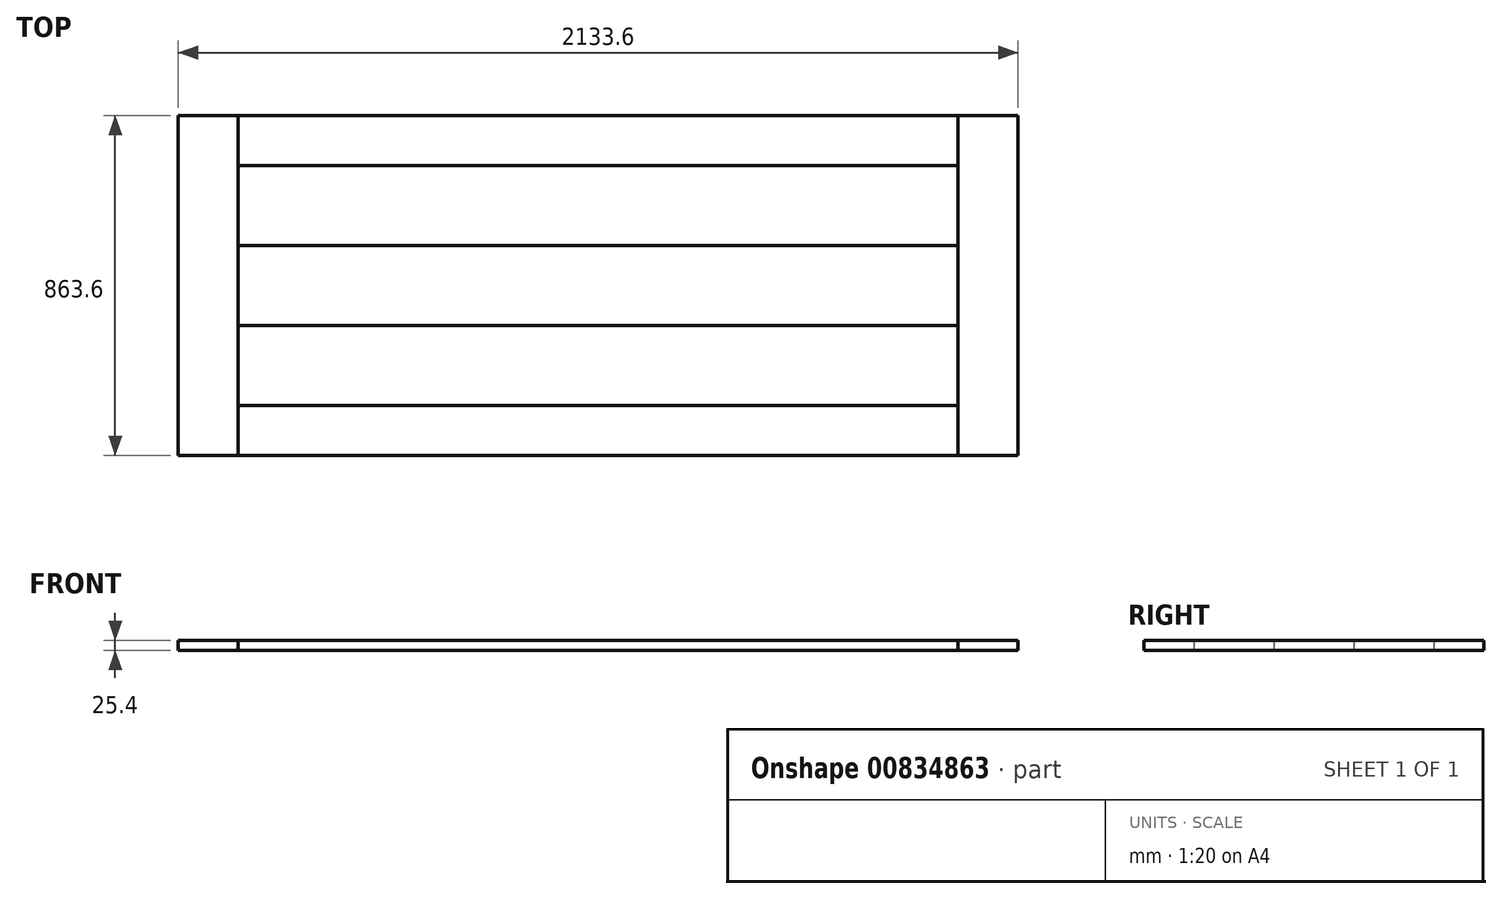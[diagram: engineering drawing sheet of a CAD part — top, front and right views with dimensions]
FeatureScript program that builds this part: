
annotation { "Feature Type Name" : "Feature", "Feature Type Description" : "" }
export const myFeature = defineFeature(function(context is Context, id is Id, definition is map)
    precondition{}
    {
        {
            var Q0;
            Q0=qCreatedBy(makeId("Top.planeOp"),FACE);
            var sketch = newSketch(context, id + "F0", { "sketchPlane" : qUnion([Q0])});
            skLineSegment(sketch, "E0.bottom", {"start": v(1066.8, -431.8) * mm, "end": v(-1066.8, -431.8) * mm});
            skLineSegment(sketch, "E0.top", {"start": v(1066.8, 431.8) * mm, "end": v(-1066.8, 431.8) * mm});
            skLineSegment(sketch, "E0.left", {"start": v(1066.8, -431.8) * mm, "end": v(1066.8, 431.8) * mm});
            skLineSegment(sketch, "E0.right", {"start": v(-1066.8, -431.8) * mm, "end": v(-1066.8, 431.8) * mm});
            skPoint(sketch, "E0.middle", {"position": v(0, 0) * mm});
            skLineSegment(sketch, "E1", {"start": v(-914.4, 431.8) * mm, "end": v(-914.4, -431.8) * mm});
            skLineSegment(sketch, "E2", {"start": v(914.4, 431.8) * mm, "end": v(914.4, -431.8) * mm});
            skLineSegment(sketch, "E3", {"start": v(-914.4, -304.8) * mm, "end": v(914.4, -304.8) * mm});
            skLineSegment(sketch, "E4", {"start": v(-914.4, -101.6) * mm, "end": v(914.4, -101.6) * mm});
            skLineSegment(sketch, "E5", {"start": v(-914.4, 101.6) * mm, "end": v(914.4, 101.6) * mm});
            skLineSegment(sketch, "E6", {"start": v(-914.4, 304.8) * mm, "end": v(914.4, 304.8) * mm});
            skSolve(sketch);
        }
        {
            var Q0;
            {var subQ4=sQuery(id+"F0.wireOp",EDGE,"E0.right");Q0=makeQuery(id+"F0.imprint","IMPRINT",FACE,{"disambiguationData":[TD([[makeQuery(id+"F0.imprint","IMPRINT",EDGE,{"derivedFrom":subQ4}),-1.0]])]});}
            var Q1;
            {var subQ0=sQuery(id+"F0.wireOp",EDGE,"E0.left");Q1=makeQuery(id+"F0.imprint","IMPRINT",FACE,{"disambiguationData":[TD([[makeQuery(id+"F0.imprint","IMPRINT",EDGE,{"derivedFrom":subQ0}),1.0]])]});}
            extrude(context, id + "F1", {"entities" : qUnion([Q0, Q1]), "depth" : 25.4 * mm, "offsetDistance" : 25.4 * mm});
        }
        {
            var Q0;
            {var subQ5=sQuery(id+"F0.wireOp",EDGE,"E6");Q0=makeQuery(id+"F0.imprint","IMPRINT",FACE,{"disambiguationData":[TD([[makeQuery(id+"F0.imprint","IMPRINT",EDGE,{"derivedFrom":subQ5}),1.0]])]});}
            var Q1;
            {var subQ0=sQuery(id+"F0.wireOp",EDGE,"E4");Q1=makeQuery(id+"F0.imprint","IMPRINT",FACE,{"disambiguationData":[TD([[makeQuery(id+"F0.imprint","IMPRINT",EDGE,{"derivedFrom":subQ0}),1.0]])]});}
            var Q2;
            {var subQ5=sQuery(id+"F0.wireOp",EDGE,"E3");Q2=makeQuery(id+"F0.imprint","IMPRINT",FACE,{"disambiguationData":[TD([[makeQuery(id+"F0.imprint","IMPRINT",EDGE,{"derivedFrom":subQ5}),-1.0]])]});}
            extrude(context, id + "F2", {"entities" : qUnion([Q0, Q1, Q2]), "depth" : 25.4 * mm, "offsetDistance" : 25.4 * mm});
        }
        {
            var Q0;
            {var subQ0=sQuery(id+"F0.wireOp",EDGE,"E5");Q0=makeQuery(id+"F0.imprint","IMPRINT",FACE,{"disambiguationData":[TD([[makeQuery(id+"F0.imprint","IMPRINT",EDGE,{"derivedFrom":subQ0}),1.0]])]});}
            var Q1;
            {var subQ0=sQuery(id+"F0.wireOp",EDGE,"E3");Q1=makeQuery(id+"F0.imprint","IMPRINT",FACE,{"disambiguationData":[TD([[makeQuery(id+"F0.imprint","IMPRINT",EDGE,{"derivedFrom":subQ0}),1.0]])]});}
            extrude(context, id + "F3", {"entities" : qUnion([Q0, Q1]), "depth" : 25.4 * mm, "offsetDistance" : 25.4 * mm});
        }
    });
